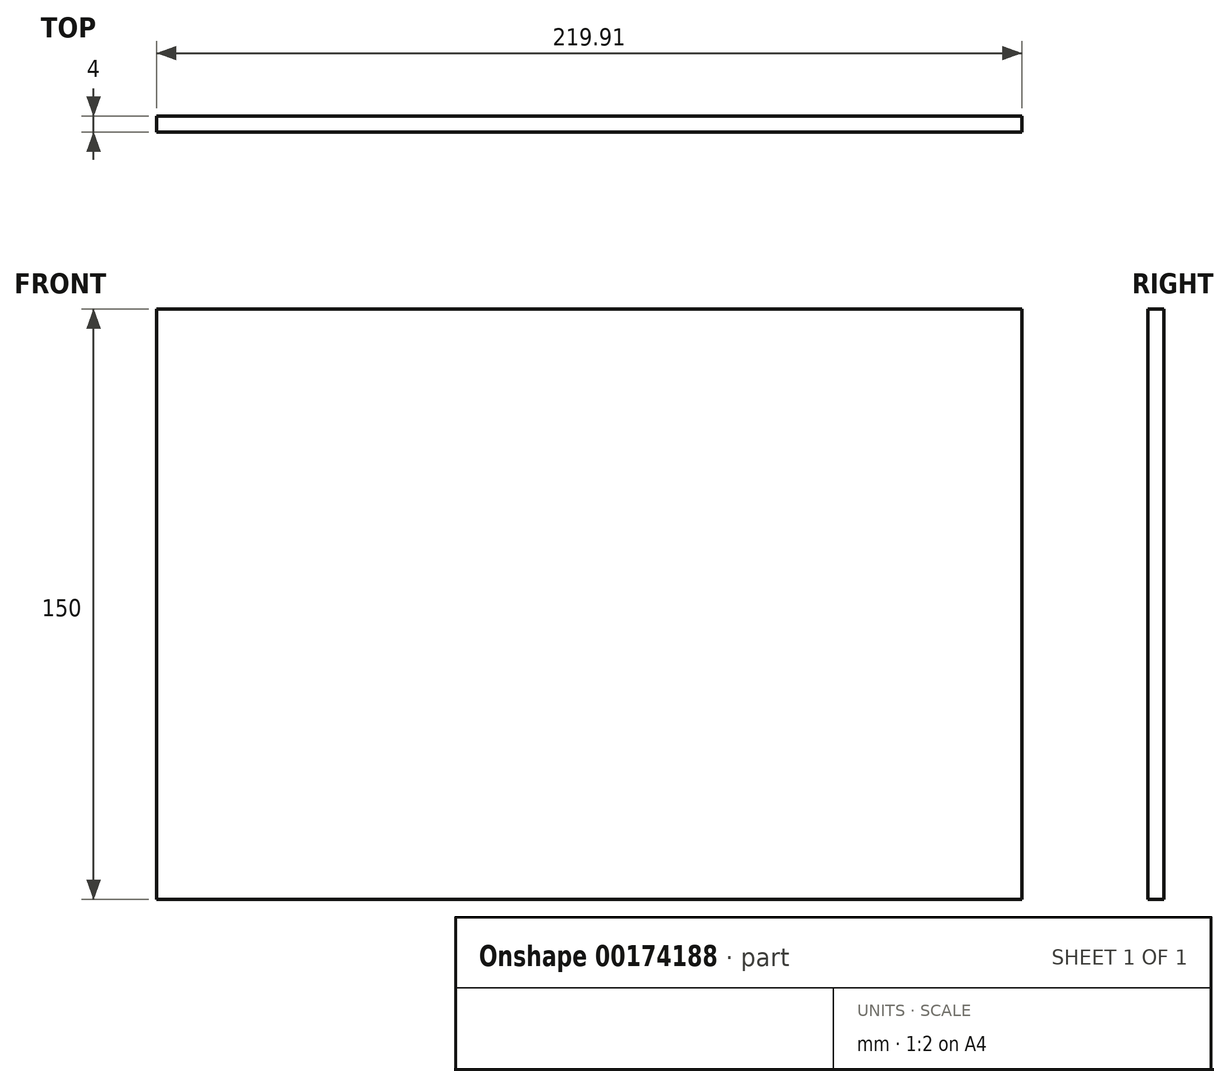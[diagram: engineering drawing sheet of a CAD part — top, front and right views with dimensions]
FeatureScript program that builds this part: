
annotation { "Feature Type Name" : "Feature", "Feature Type Description" : "" }
export const myFeature = defineFeature(function(context is Context, id is Id, definition is map)
    precondition{}
    {
        {
            var Q0;
            Q0=qCreatedBy(makeId("Front.planeOp"),FACE);
            var sketch = newSketch(context, id + "F0", { "sketchPlane" : qUnion([Q0])});
            skLineSegment(sketch, "E0.bottom", {"start": v(0, 0) * mm, "end": v(219.9, 0) * mm});
            skLineSegment(sketch, "E0.top", {"start": v(0, 150) * mm, "end": v(219.9, 150) * mm});
            skLineSegment(sketch, "E0.left", {"start": v(0, 0) * mm, "end": v(0, 150) * mm});
            skLineSegment(sketch, "E0.right", {"start": v(219.9, 0) * mm, "end": v(219.9, 150) * mm});
            skSolve(sketch);
        }
        {
            var Q0;
            Q0 = qSketchRegion(id + "F0", true);
            extrude(context, id + "F1", {"entities" : qUnion([Q0]), "depth" : 4 * mm});
        }
    });
